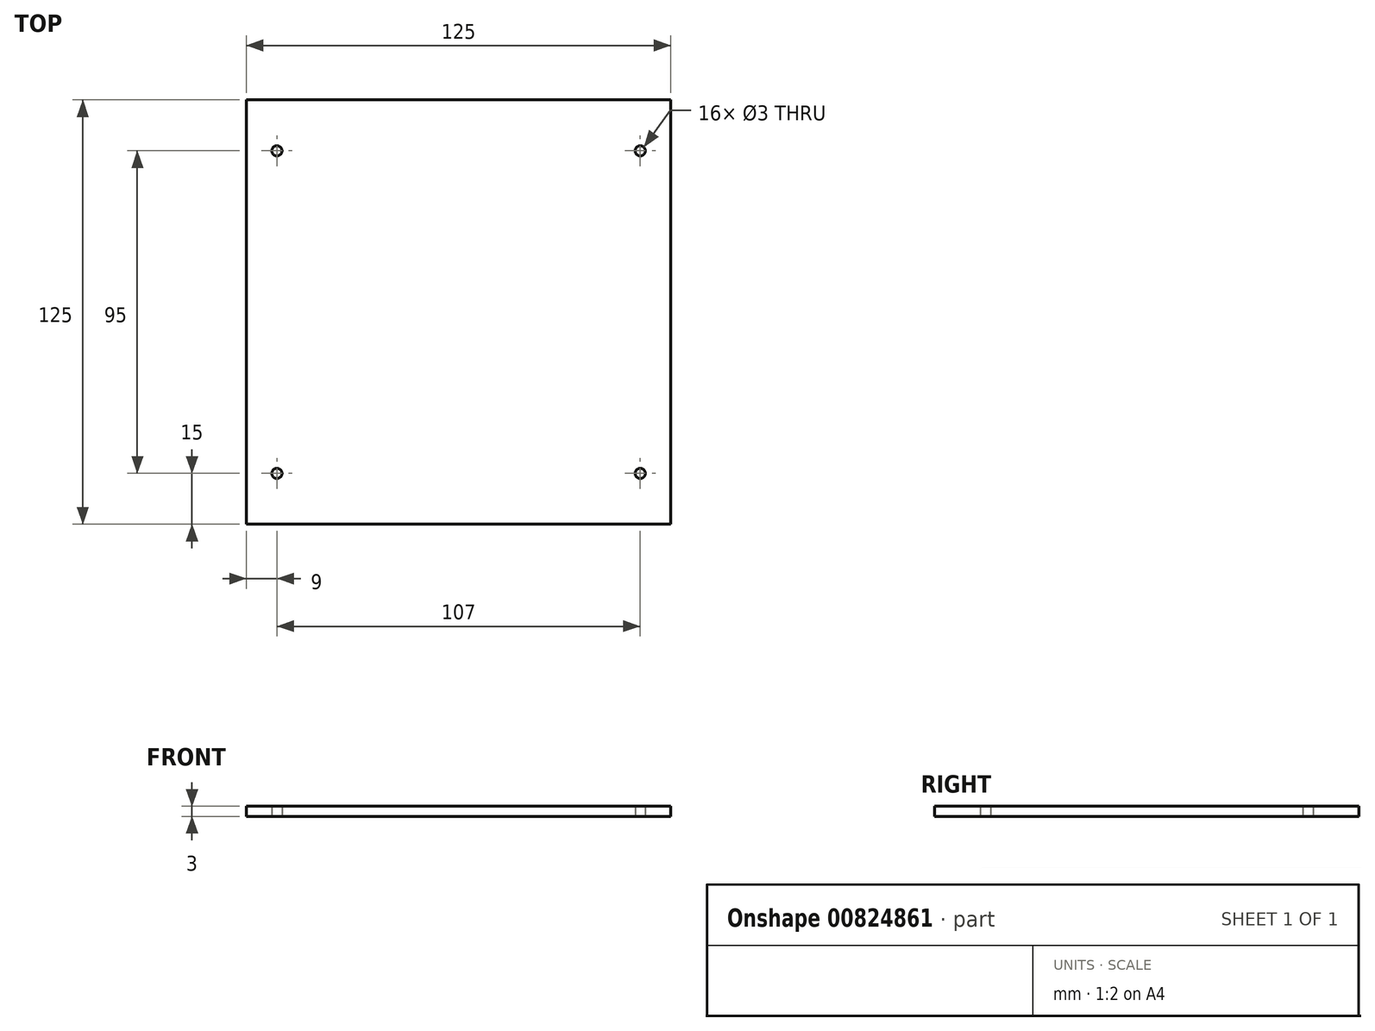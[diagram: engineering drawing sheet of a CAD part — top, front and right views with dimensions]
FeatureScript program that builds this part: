
annotation { "Feature Type Name" : "Feature", "Feature Type Description" : "" }
export const myFeature = defineFeature(function(context is Context, id is Id, definition is map)
    precondition{}
    {
        {
            var Q0;
            Q0=qCreatedBy(makeId("Top.planeOp"),FACE);
            var sketch = newSketch(context, id + "F0", { "sketchPlane" : qUnion([Q0])});
            skLineSegment(sketch, "E0.bottom", {"start": v(62.5, 62.5) * mm, "end": v(-62.5, 62.5) * mm});
            skLineSegment(sketch, "E0.top", {"start": v(62.5, -62.5) * mm, "end": v(-62.5, -62.5) * mm});
            skLineSegment(sketch, "E0.left", {"start": v(62.5, 62.5) * mm, "end": v(62.5, -62.5) * mm});
            skLineSegment(sketch, "E0.right", {"start": v(-62.5, 62.5) * mm, "end": v(-62.5, -62.5) * mm});
            skPoint(sketch, "E0.middle", {"position": v(0, 0) * mm});
            skCircle(sketch, "E1", {"center": v(-53.5, 47.5) * mm, "radius": 1.5 * mm});
            skCircle(sketch, "E2", {"center": v(-53.5, -47.5) * mm, "radius": 1.5 * mm});
            skCircle(sketch, "E3.MirrorC", {"center": v(53.5, 47.5) * mm, "radius": 1.5 * mm});
            skCircle(sketch, "E4.MirrorC", {"center": v(53.5, -47.5) * mm, "radius": 1.5 * mm});
            skSolve(sketch);
        }
        {
            var Q0;
            Q0=makeQuery(id+"F0.imprint","IMPRINT",FACE,{"disambiguationData":[TD([[makeQuery(id+"F0.imprint","IMPRINT",EDGE,{"derivedFrom":sQuery(id+"F0.wireOp",EDGE,"E0.bottom")}),1.0]])]});
            extrude(context, id + "F1", {"entities" : qUnion([Q0]), "depth" : 3 * mm, "offsetDistance" : 25 * mm});
        }
    });
